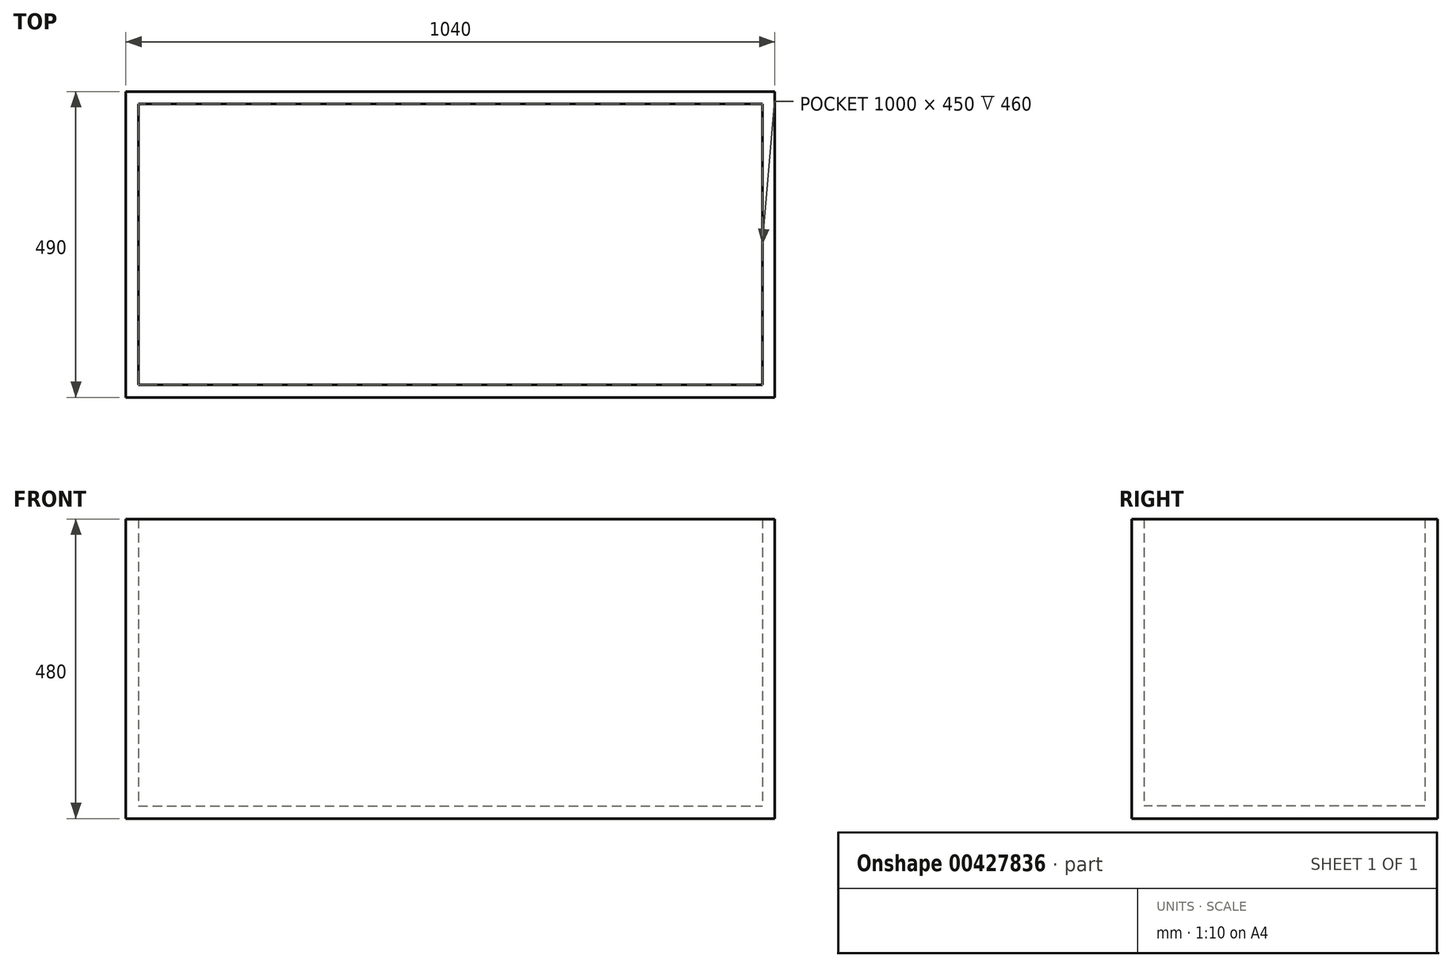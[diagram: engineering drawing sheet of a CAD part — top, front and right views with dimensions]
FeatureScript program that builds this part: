
annotation { "Feature Type Name" : "Feature", "Feature Type Description" : "" }
export const myFeature = defineFeature(function(context is Context, id is Id, definition is map)
    precondition{}
    {
        {
            var Q0;
            Q0=qCreatedBy(makeId("Front.planeOp"),FACE);
            var sketch = newSketch(context, id + "F0", { "sketchPlane" : qUnion([Q0])});
            skLineSegment(sketch, "E0.bottom", {"start": v(-553.97, 314.67) * mm, "end": v(486.03, 314.67) * mm});
            skLineSegment(sketch, "E0.top", {"start": v(-553.97, -165.33) * mm, "end": v(486.03, -165.33) * mm});
            skLineSegment(sketch, "E0.left", {"start": v(-553.97, 314.67) * mm, "end": v(-553.97, -165.33) * mm});
            skLineSegment(sketch, "E0.right", {"start": v(486.03, 314.67) * mm, "end": v(486.03, -165.33) * mm});
            skSolve(sketch);
        }
        {
            var Q0;
            Q0=makeQuery(id+"F0.imprint","IMPRINT",FACE,{"disambiguationData":[TD([[makeQuery(id+"F0.imprint","IMPRINT",EDGE,{"derivedFrom":sQuery(id+"F0.wireOp",EDGE,"E0.bottom")}),-1.0]])]});
            extrude(context, id + "F1", {"entities" : qUnion([Q0]), "oppositeDirection" : true, "depth" : 490 * mm});
        }
        {
            var Q0;
            Q0=makeQuery(id+"F1.opExtrude","SWEPT_FACE",FACE,{"disambiguationData":[OSD([sQuery(id+"F0.wireOp",EDGE,"E0.bottom")])]});
            shell(context, id + "F2", {"entities" : qUnion([Q0]), "thickness" : 20 * mm});
        }
    });
